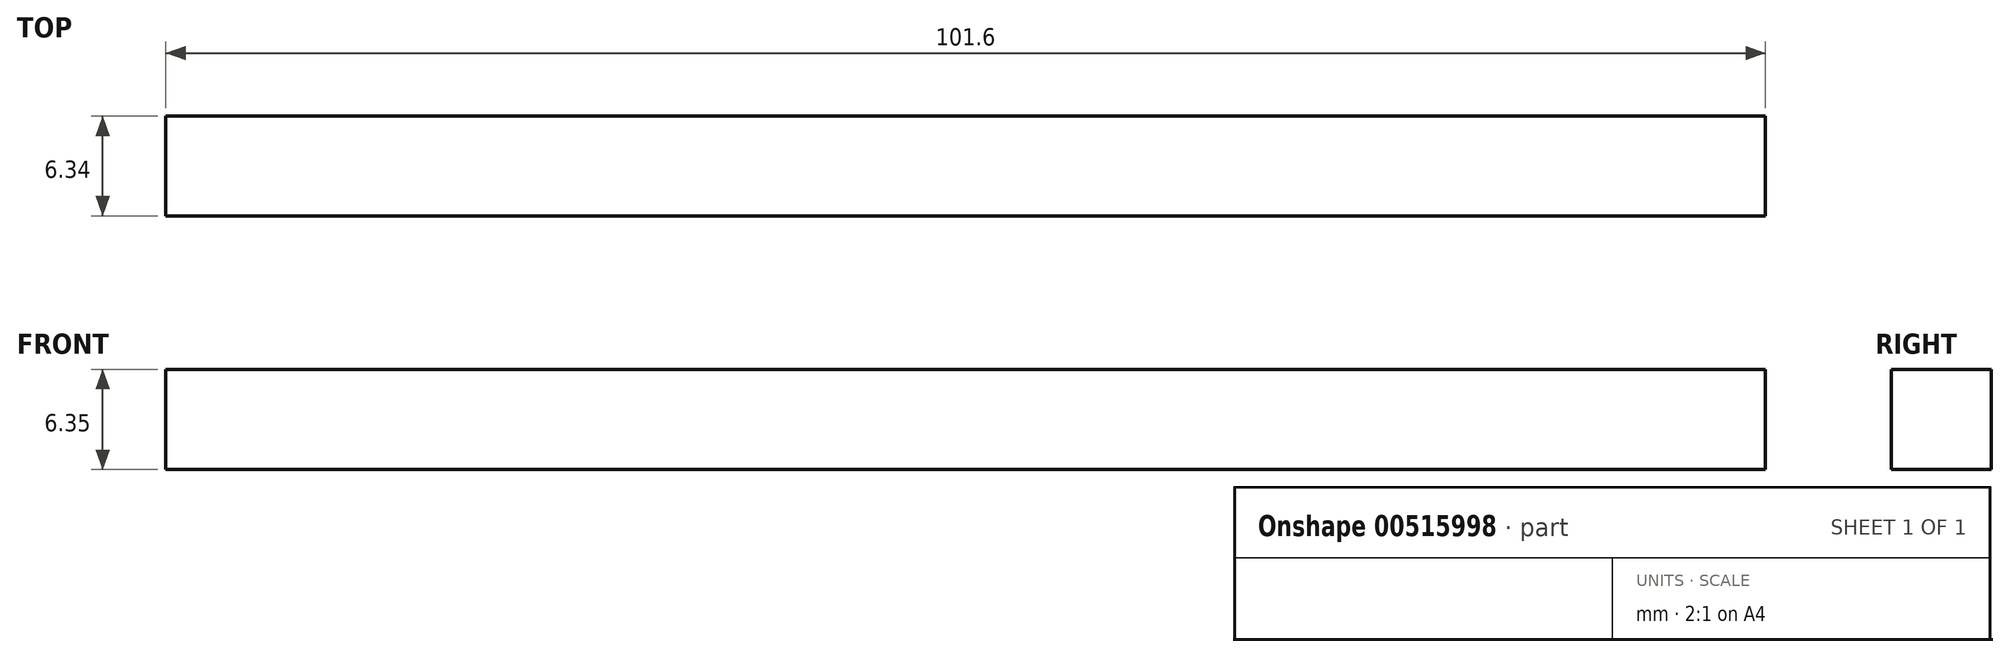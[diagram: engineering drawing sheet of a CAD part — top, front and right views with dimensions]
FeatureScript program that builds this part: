
annotation { "Feature Type Name" : "Feature", "Feature Type Description" : "" }
export const myFeature = defineFeature(function(context is Context, id is Id, definition is map)
    precondition{}
    {
        {
            var Q0;
            Q0=qCreatedBy(makeId("Top.planeOp"),FACE);
            var sketch = newSketch(context, id + "F0", { "sketchPlane" : qUnion([Q0])});
            skLineSegment(sketch, "E0.bottom", {"start": v(50.8, 3.18) * mm, "end": v(-50.8, 3.18) * mm});
            skLineSegment(sketch, "E0.top", {"start": v(50.8, -3.18) * mm, "end": v(-50.8, -3.18) * mm});
            skLineSegment(sketch, "E0.left", {"start": v(50.8, 3.18) * mm, "end": v(50.8, -3.18) * mm});
            skLineSegment(sketch, "E0.right", {"start": v(-50.8, 3.18) * mm, "end": v(-50.8, -3.18) * mm});
            skPoint(sketch, "E0.middle", {"position": v(0, 0) * mm});
            skSolve(sketch);
        }
        {
            var Q0;
            Q0=makeQuery(id+"F0.imprint","IMPRINT",FACE,{"disambiguationData":[TD([[makeQuery(id+"F0.imprint","IMPRINT",EDGE,{"derivedFrom":sQuery(id+"F0.wireOp",EDGE,"E0.bottom")}),1.0]])]});
            extrude(context, id + "F1", {"entities" : qUnion([Q0]), "depth" : 6.35 * mm, "offsetDistance" : 25.4 * mm});
        }
    });
